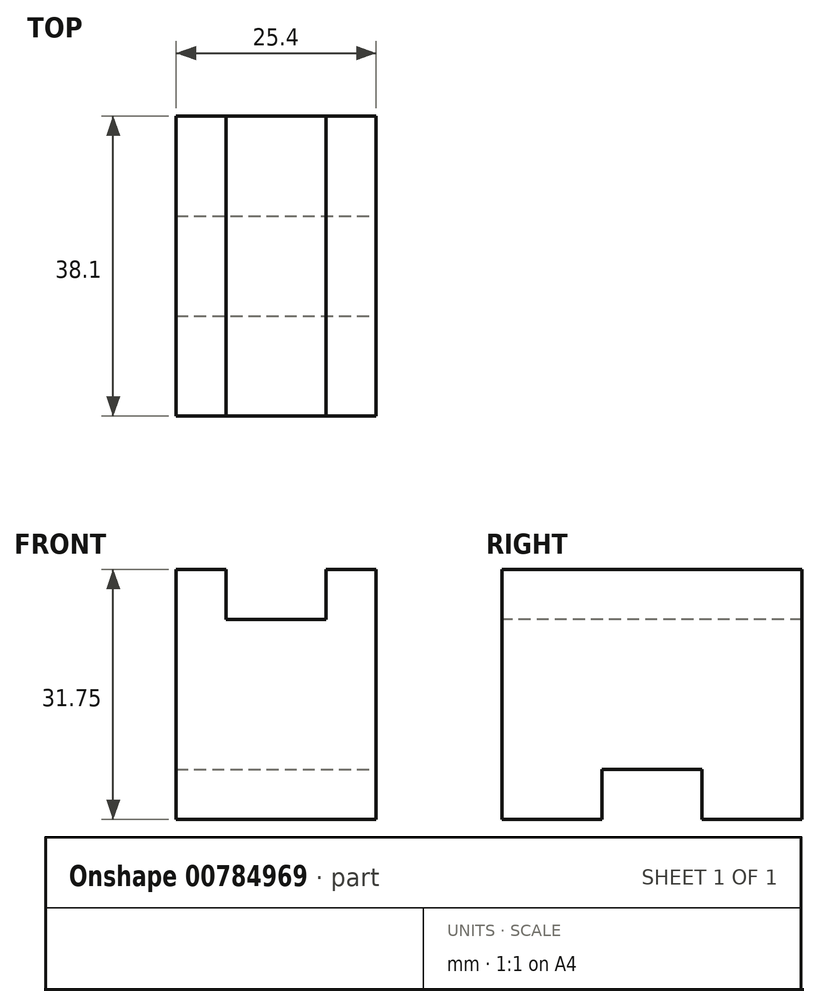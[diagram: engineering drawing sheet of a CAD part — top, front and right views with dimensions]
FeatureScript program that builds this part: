
annotation { "Feature Type Name" : "Feature", "Feature Type Description" : "" }
export const myFeature = defineFeature(function(context is Context, id is Id, definition is map)
    precondition{}
    {
        {
            var Q0;
            Q0=qCreatedBy(makeId("Front.planeOp"),FACE);
            var sketch = newSketch(context, id + "F0", { "sketchPlane" : qUnion([Q0])});
            skLineSegment(sketch, "E0", {"start": v(0, 0) * mm, "end": v(25.4, 0) * mm});
            skLineSegment(sketch, "E1", {"start": v(25.4, 0) * mm, "end": v(25.4, 31.75) * mm});
            skLineSegment(sketch, "E2", {"start": v(25.4, 31.75) * mm, "end": v(0, 31.75) * mm});
            skLineSegment(sketch, "E3", {"start": v(0, 0) * mm, "end": v(0, 31.75) * mm});
            skSolve(sketch);
        }
        {
            var Q0;
            Q0=makeQuery(id+"F0.imprint","IMPRINT",FACE,{"disambiguationData":[TD([[makeQuery(id+"F0.imprint","IMPRINT",EDGE,{"derivedFrom":sQuery(id+"F0.wireOp",EDGE,"E0")}),1.0]])]});
            extrude(context, id + "F1", {"entities" : qUnion([Q0]), "depth" : 31.75 * mm, "offsetDistance" : 25.4 * mm});
        }
        {
            var Q0;
            Q0=makeQuery(id+"F1.opExtrude","CAP_FACE",FACE,{"disambiguationData":[OSD([sQuery(id+"F0.wireOp",EDGE,"E0"),sQuery(id+"F0.wireOp",EDGE,"E1"),sQuery(id+"F0.wireOp",EDGE,"E2"),sQuery(id+"F0.wireOp",EDGE,"E3")])],"isStart":false});
            var sketch = newSketch(context, id + "F2", { "sketchPlane" : qUnion([Q0])});
            skLineSegment(sketch, "E4", {"start": v(0, 31.75) * mm, "end": v(6.35, 31.75) * mm});
            skLineSegment(sketch, "E5", {"start": v(25.4, 31.75) * mm, "end": v(19.05, 31.75) * mm});
            skLineSegment(sketch, "E6", {"start": v(19.05, 31.75) * mm, "end": v(19.05, 25.4) * mm});
            skLineSegment(sketch, "E7", {"start": v(19.05, 25.4) * mm, "end": v(6.36, 25.4) * mm});
            skLineSegment(sketch, "E8", {"start": v(6.35, 31.75) * mm, "end": v(6.36, 25.4) * mm});
            skSolve(sketch);
        }
        {
            var Q0;
            Q0 = qSketchRegion(id + "F2", true);
            var Q1;
            {var subQ0=sQuery(id+"F2.wireOp",EDGE,"E6");Q1=makeQuery(id+"F2.imprint","IMPRINT",FACE,{"disambiguationData":[TD([[makeQuery(id+"F2.imprint","IMPRINT",EDGE,{"derivedFrom":subQ0}),-1.0]])]});}
            extrude(context, id + "F3", {"entities" : qUnion([Q0, Q1]), "operationType" : NewBodyOperationType.REMOVE, "oppositeDirection" : true, "depth" : 31.75 * mm, "offsetDistance" : 25.4 * mm});
        }
        {
            var Q0;
            Q0 = qSketchRegion(id + "Fn0wNaYLdAiS6Ou_1", true);
            var Q1;
            Q1=makeQuery(id+"F1.opExtrude","CAP_FACE",FACE,{"disambiguationData":[OSD([sQuery(id+"F0.wireOp",EDGE,"E0"),sQuery(id+"F0.wireOp",EDGE,"E1"),sQuery(id+"F0.wireOp",EDGE,"E2"),sQuery(id+"F0.wireOp",EDGE,"E3")])],"isStart":false});
            extrude(context, id + "F4", {"entities" : qUnion([Q0, Q1]), "operationType" : NewBodyOperationType.ADD, "depth" : 6.35 * mm, "offsetDistance" : 25.4 * mm});
        }
        {
            var Q0;
            {var subQ0=sQuery(id+"F0.wireOp",EDGE,"E1");Q0=makeQuery(id+"F4.boolean.opBoolean","MERGE",FACE,{"derivedFrom":[makeQuery(id+"F1.opExtrude","SWEPT_FACE",FACE,{"disambiguationData":[OSD([subQ0])]}),makeQuery(id+"F4.opExtrude","SWEPT_FACE",FACE,{"disambiguationData":[OSD([subQ0])]})]});}
            var sketch = newSketch(context, id + "F5", { "sketchPlane" : qUnion([Q0])});
            skLineSegment(sketch, "E9", {"start": v(-38.1, 0) * mm, "end": v(-25.4, 0) * mm});
            skLineSegment(sketch, "E10", {"start": v(-25.4, 0) * mm, "end": v(-25.4, 6.35) * mm});
            skLineSegment(sketch, "E11", {"start": v(-25.4, 6.35) * mm, "end": v(-12.7, 6.35) * mm});
            skLineSegment(sketch, "E12", {"start": v(-12.7, 6.35) * mm, "end": v(-12.7, 0) * mm});
            skSolve(sketch);
        }
        {
            var Q0;
            {var subQ0=sQuery(id+"F5.wireOp",EDGE,"E10");Q0=makeQuery(id+"F5.imprint","IMPRINT",FACE,{"disambiguationData":[TD([[makeQuery(id+"F5.imprint","IMPRINT",EDGE,{"derivedFrom":subQ0}),-1.0]])]});}
            extrude(context, id + "F6", {"entities" : qUnion([Q0]), "operationType" : NewBodyOperationType.REMOVE, "oppositeDirection" : true, "depth" : 25.4 * mm, "offsetDistance" : 25.4 * mm});
        }
    });
